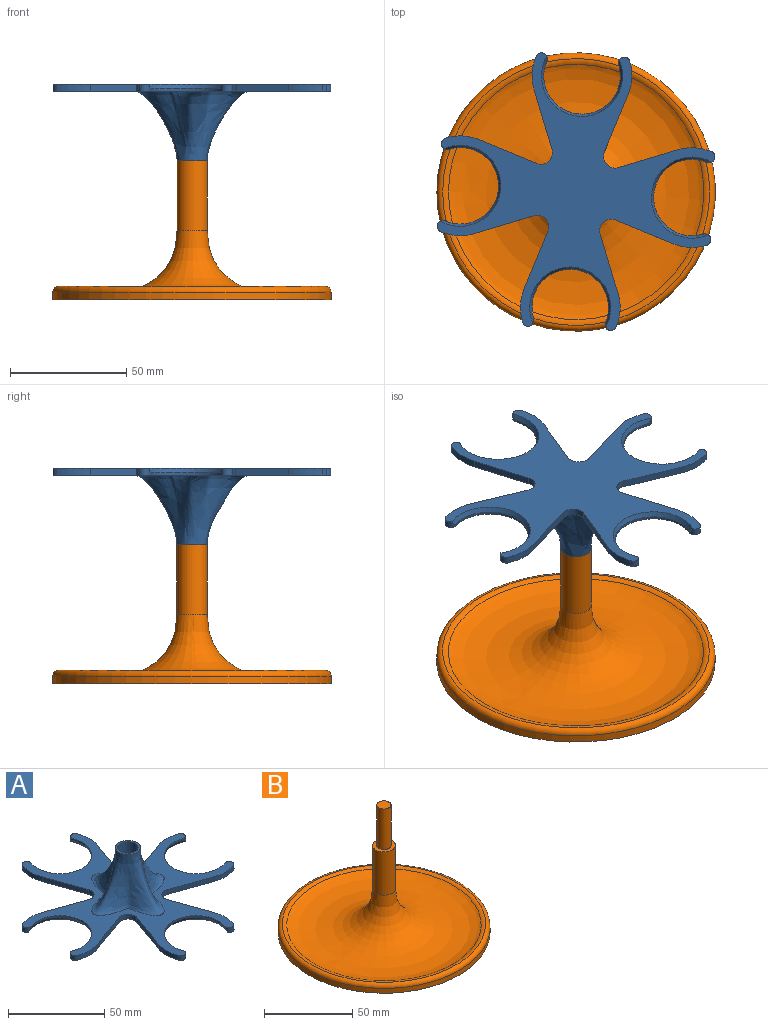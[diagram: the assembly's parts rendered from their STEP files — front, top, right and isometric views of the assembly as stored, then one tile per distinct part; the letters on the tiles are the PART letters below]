
ASSEMBLY  parts=2 mates=1
PART A: 42 faces, bbox 118.3x118.3x33.2 mm
  f0: plane 118.28x118.28mm, normal (0,0,1), area 3009.3mm2, adj f1,f2,f3,f4,f5,f6,f7,f8
  f1: cylinder r=16.5mm len=33mm, axis (0,0,-1), area 63.4mm2, adj f0,f2,f32,f36
  f2: cylinder r=2.5mm len=4.85mm, axis (0,0,-1), area 21.4mm2, adj f0,f1,f3,f33,f36
  f3: cylinder r=21.5mm len=14.59mm, axis (0,0,-1), area 44.7mm2, adj f0,f2,f4,f33
  f4: plane 25.08x8.94mm, normal (-0.34,0.94,0), area 79.9mm2, adj f0,f3,f5,f33
  f5: cylinder r=5mm len=6.68mm, axis (0,0,-1), area 33.8mm2, adj f0,f4,f6,f33
  f6: plane 25.08x8.94mm, normal (0.94,-0.34,0), area 79.9mm2, adj f0,f5,f7,f33
  f7: cylinder r=21.5mm len=14.59mm, axis (0,0,-1), area 44.7mm2, adj f0,f6,f8,f33
  f8: cylinder r=2.5mm len=4.85mm, axis (0,0,-1), area 21.4mm2, adj f0,f7,f9,f33,f34
  f9: cylinder r=16.5mm len=33mm, axis (0,0,-1), area 63.4mm2, adj f0,f8,f10,f34
  f10: cylinder r=2.5mm len=4.85mm, axis (0,0,-1), area 21.4mm2, adj f0,f9,f11,f33,f34
  f11: cylinder r=21.5mm len=14.59mm, axis (0,0,-1), area 44.7mm2, adj f0,f10,f12,f33
  f12: plane 25.08x8.94mm, normal (-0.94,-0.34,0), area 79.9mm2, adj f0,f11,f13,f33
  f13: cylinder r=5mm len=6.68mm, axis (0,0,-1), area 33.8mm2, adj f0,f12,f14,f33
  f14: plane 25.08x8.94mm, normal (0.34,0.94,0), area 79.9mm2, adj f0,f13,f15,f33
  f15: cylinder r=21.5mm len=14.59mm, axis (0,0,-1), area 44.7mm2, adj f0,f14,f16,f33
  f16: cylinder r=2.5mm len=4.85mm, axis (0,0,-1), area 21.4mm2, adj f0,f15,f17,f33,f35
  f17: cylinder r=16.5mm len=33mm, axis (0,0,-1), area 63.4mm2, adj f0,f16,f18,f35
  f18: cylinder r=2.5mm len=4.85mm, axis (0,0,-1), area 21.4mm2, adj f0,f17,f19,f33,f35
  f19: cylinder r=21.5mm len=14.59mm, axis (0,0,-1), area 44.7mm2, adj f0,f18,f20,f33
  f20: plane 25.08x8.94mm, normal (0.34,-0.94,0), area 79.9mm2, adj f0,f19,f21,f33
  f21: cylinder r=5mm len=6.68mm, axis (0,0,-1), area 33.8mm2, adj f0,f20,f22,f33
  f22: plane 25.08x8.94mm, normal (-0.94,0.34,0), area 79.9mm2, adj f0,f21,f23,f33
  f23: cylinder r=21.5mm len=14.59mm, axis (0,0,-1), area 44.7mm2, adj f0,f22,f24,f33
  f24: cylinder r=2.5mm len=4.85mm, axis (0,0,-1), area 21.4mm2, adj f0,f23,f25,f33,f37
  f25: cylinder r=16.5mm len=33mm, axis (0,0,-1), area 63.4mm2, adj f0,f24,f26,f37
  f26: cylinder r=2.5mm len=4.85mm, axis (0,0,-1), area 21.4mm2, adj f0,f25,f27,f33,f37
  f27: cylinder r=21.5mm len=14.59mm, axis (0,0,-1), area 44.7mm2, adj f0,f26,f28,f33
  f28: plane 25.08x8.94mm, normal (0.94,0.34,0), area 79.9mm2, adj f0,f27,f29,f33
  f29: cylinder r=5mm len=6.68mm, axis (0,0,-1), area 33.8mm2, adj f0,f28,f30,f33
  f30: plane 25.08x8.94mm, normal (-0.34,-0.94,0), area 79.9mm2, adj f0,f29,f31,f33
  f31: cylinder r=21.5mm len=14.59mm, axis (0,0,-1), area 44.7mm2, adj f0,f30,f32,f33
  f32: cylinder r=2.5mm len=4.85mm, axis (0,0,-1), area 21.4mm2, adj f0,f1,f31,f33,f36
  f33: plane 118.03x118.03mm, normal (0,0,-1), area 3843.8mm2, adj f2,f3,f4,f5,f6,f7,f8,f10
  f34: cone r=17.5mm half-angle=26.6deg, axis (0,0,-1), area 150.2mm2, adj f8,f9,f10,f33
  f35: cone r=17.5mm half-angle=26.6deg, axis (0,0,-1), area 150.2mm2, adj f16,f17,f18,f33
  f36: cone r=17.5mm half-angle=26.6deg, axis (0,0,-1), area 150.2mm2, adj f1,f2,f32,f33
  f37: cone r=17.5mm half-angle=26.6deg, axis (0,0,-1), area 150.2mm2, adj f24,f25,f26,f33
  f38: plane 13.19x13.19mm, normal (0,0,1), area 46.1mm2, adj f39,f41
  f39: bspline ~50x50mm, area 2480.2mm2, adj f0,f38
  f40: plane 10.5x10.5mm, normal (0,0,1), area 86.6mm2, adj f41
  f41: cylinder r=5.25mm len=30mm, axis (0,0,1), area 989.6mm2, adj f38,f40
PART B: 9 faces, bbox 131.1x131.1x88 mm
  f0: plane 120x120mm, normal (0,0,-1), area 11309.7mm2, adj f1
  f1: cylinder r=60mm len=120mm, axis (0,0,-1), area 1241.8mm2, adj f0,f2
  f2: torus R=57.5mm, axis (0,0,-1), area 1458mm2, adj f1,f3
  f3: torus R=57.5mm, axis (0,0,-1), area 941.2mm2, adj f2,f4
  f4: revolved ~110x110mm, area 10439.5mm2, adj f3,f5
  f5: cylinder r=6.5mm len=30mm, axis (0,0,-1), area 1225.2mm2, adj f4,f6
  f6: plane 13x13mm, normal (0,0,1), area 82.5mm2, adj f5,f7
  f7: cylinder r=4mm len=28mm, axis (0,0,-1), area 703.7mm2, adj f6,f8
  f8: plane 8x8mm, normal (0,0,1), area 50.3mm2, adj f7
PLACE A rot(axis=(0.69,-0.72,0),180deg) t=(0,0,93)mm
PLACE B at identity fixed
MATE revolute B.f7 <-> A.f41  axis (0,0,-1) through (0,0,60)mm
